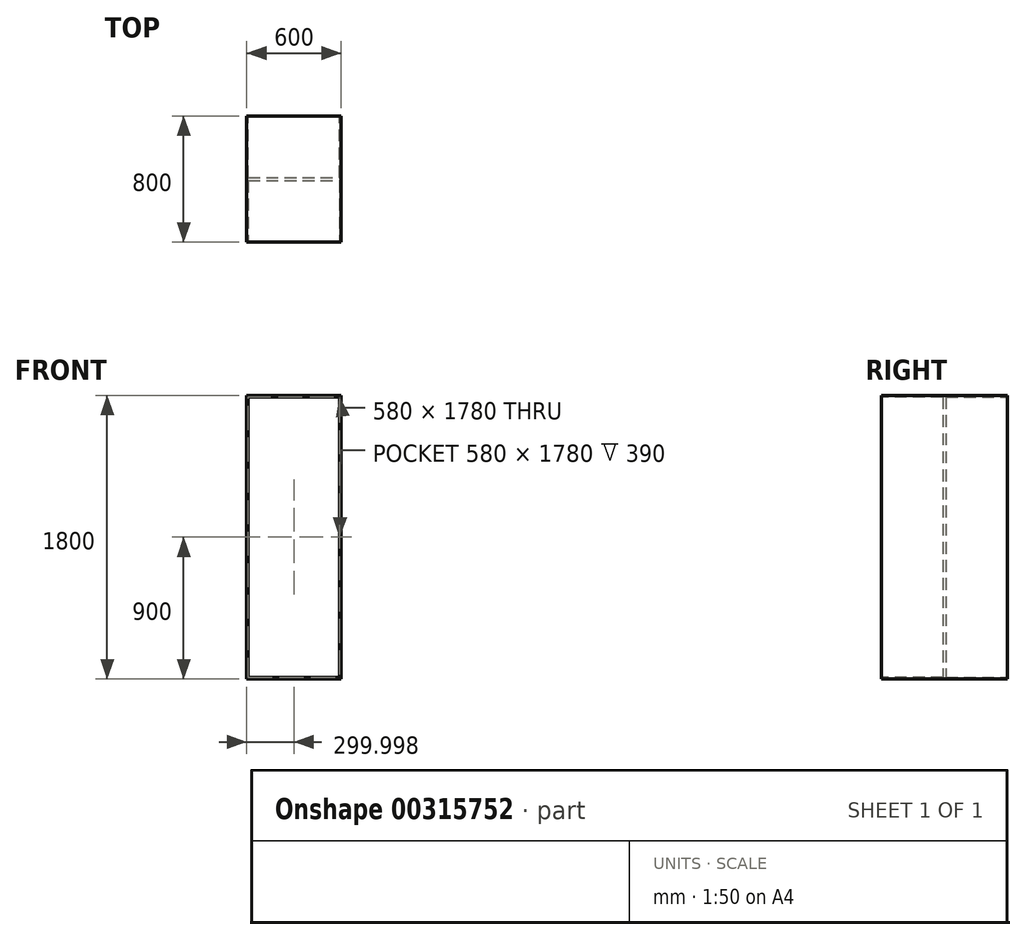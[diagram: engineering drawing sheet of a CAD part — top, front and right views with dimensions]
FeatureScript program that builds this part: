
annotation { "Feature Type Name" : "Feature", "Feature Type Description" : "" }
export const myFeature = defineFeature(function(context is Context, id is Id, definition is map)
    precondition{}
    {
        {
            var Q0;
            Q0=qCreatedBy(makeId("Top.planeOp"),FACE);
            var sketch = newSketch(context, id + "F0", { "sketchPlane" : qUnion([Q0])});
            skLineSegment(sketch, "E0.bottom", {"start": v(-109.21, 263.79) * mm, "end": v(490.79, 263.79) * mm});
            skLineSegment(sketch, "E0.top", {"start": v(-109.21, -136.21) * mm, "end": v(490.79, -136.21) * mm});
            skLineSegment(sketch, "E0.left", {"start": v(-109.21, 263.79) * mm, "end": v(-109.21, -136.21) * mm});
            skLineSegment(sketch, "E0.right", {"start": v(490.79, 263.79) * mm, "end": v(490.79, -136.21) * mm});
            skSolve(sketch);
        }
        {
            var Q0;
            Q0=makeQuery(id+"F0.imprint","IMPRINT",FACE,{"disambiguationData":[TD([[makeQuery(id+"F0.imprint","IMPRINT",EDGE,{"derivedFrom":sQuery(id+"F0.wireOp",EDGE,"E0.bottom")}),-1.0]])]});
            extrude(context, id + "F1", {"entities" : qUnion([Q0]), "depth" : 1800 * mm});
        }
        {
            var Q0;
            Q0=makeQuery(id+"F1.opExtrude","SWEPT_FACE",FACE,{"disambiguationData":[OSD([sQuery(id+"F0.wireOp",EDGE,"E0.top")])]});
            var sketch = newSketch(context, id + "F2", { "sketchPlane" : qUnion([Q0])});
            skLineSegment(sketch, "E1.0", {"start": v(-99.21, 10) * mm, "end": v(480.79, 10) * mm});
            skLineSegment(sketch, "E1.1", {"start": v(-99.21, 1790) * mm, "end": v(-99.21, 10) * mm});
            skLineSegment(sketch, "E1.2", {"start": v(480.79, 1790) * mm, "end": v(-99.21, 1790) * mm});
            skLineSegment(sketch, "E1.3", {"start": v(480.79, 10) * mm, "end": v(480.79, 1790) * mm});
            skSolve(sketch);
        }
        {
            var Q0;
            Q0=makeQuery(id+"F2.imprint","IMPRINT",FACE,{"disambiguationData":[TD([[makeQuery(id+"F2.imprint","IMPRINT",EDGE,{"derivedFrom":sQuery(id+"F2.wireOp",EDGE,"E1.0")}),1.0]])]});
            extrude(context, id + "F3", {"entities" : qUnion([Q0]), "operationType" : NewBodyOperationType.REMOVE, "oppositeDirection" : true, "depth" : 390 * mm});
        }
        {
            var Q0;
            Q0=makeQuery(id+"F1.opExtrude","SWEPT_BODY",BODY,{"disambiguationData":[OSD([sQuery(id+"F0.wireOp",EDGE,"E0.bottom"),sQuery(id+"F0.wireOp",EDGE,"E0.top"),sQuery(id+"F0.wireOp",EDGE,"E0.left"),sQuery(id+"F0.wireOp",EDGE,"E0.right")])]});
            var Q1;
            Q1=makeQuery(id+"F1.opExtrude","SWEPT_FACE",FACE,{"disambiguationData":[OSD([sQuery(id+"F0.wireOp",EDGE,"E0.bottom")])]});
            mirror(context, id + "F4", {"operationType" : NewBodyOperationType.ADD, "entities" : qUnion([Q0]), "mirrorPlane" : qUnion([Q1])});
        }
    });
